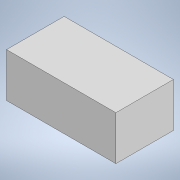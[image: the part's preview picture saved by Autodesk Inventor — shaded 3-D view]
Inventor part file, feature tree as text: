
AUTODESK INVENTOR PART (.ipt)
format: ipt  version: 2020 (Build 240168000, 168)  size: 85,504 bytes
history: native  units: mm
features: extrude x1, sketch x1
ambient origin geometry x8: Origin, YZ Plane, XZ Plane, XY Plane, X Axis, Y Axis, Z Axis, Center Point
bodies: Volumenkörper1 (feature_tree)
feature tree (2):
  extrude  "Extrusion1"  Depth=300.0mm
  sketch  "Skizze1"  dims[d0=570.0mm d1=300.0mm d2=230.0mm d3=0.0mm]
